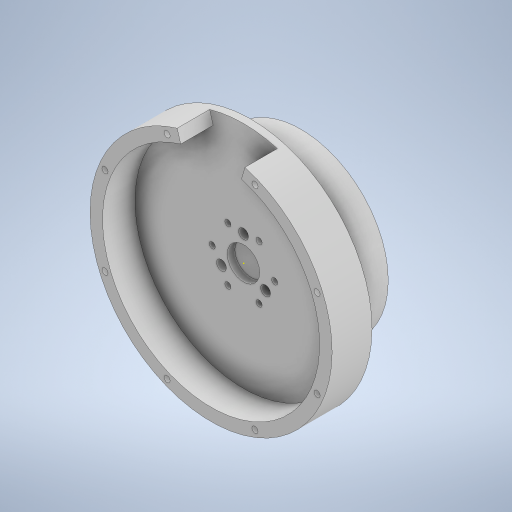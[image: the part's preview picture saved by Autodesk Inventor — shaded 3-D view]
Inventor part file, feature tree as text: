
AUTODESK INVENTOR PART (.ipt)
format: ipt  version: 2024.3 (Build 283343000, 343)  size: 345,088 bytes
history: native  units: mm
features: sketch x10, extrude x6, hole x3, other x1
ambient origin geometry x8: Origin, YZ Plane, XZ Plane, XY Plane, X Axis, Y Axis, Z Axis, Center Point
bodies: Body1 (feature_tree)
feature tree (20):
  other  "ソリッド1"
  extrude  "押し出し1"  Depth=97.0mm
  hole  "穴1"  [1 undecoded]
  hole  "穴2"  [1 undecoded]
  hole  "穴3"  [1 undecoded]
  extrude  "押し出し2"  Depth=40.0mm TaperAngle=360.0deg
  extrude  "押し出し3"  Depth=25.0mm
  extrude  "押し出し4"  TaperAngle=30.0deg  [1 undecoded]
  extrude  "押し出し5"  Depth=60.0mm TaperAngle=360.0deg
  extrude  "押し出し6"  Depth=20.4mm
  sketch  "スケッチ10"
  sketch  "スケッチ1"
  sketch  "スケッチ2"
  sketch  "スケッチ3"
  sketch  "スケッチ4"
  sketch  "スケッチ5"
  sketch  "スケッチ6"
  sketch  "スケッチ7"
  sketch  "スケッチ8"
  sketch  "スケッチ9"
note: 4 required parameter values undecoded (feature->parameter linkage not recoverable at this tier; creation-order binding heuristic only, values carry confidence <= 0.55)
